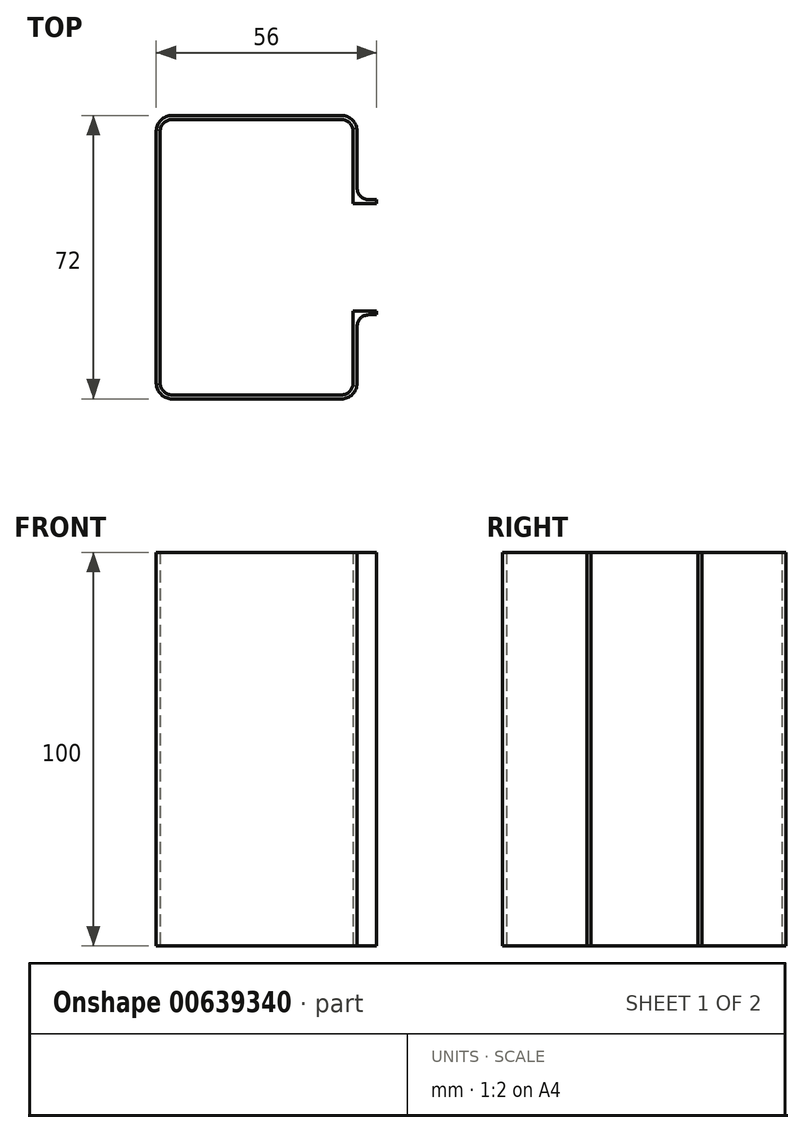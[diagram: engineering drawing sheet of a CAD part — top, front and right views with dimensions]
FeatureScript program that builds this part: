
annotation { "Feature Type Name" : "Feature", "Feature Type Description" : "" }
export const myFeature = defineFeature(function(context is Context, id is Id, definition is map)
    precondition{}
    {
        {
            var Q0;
            Q0=qCreatedBy(makeId("Top.planeOp"),FACE);
            var sketch = newSketch(context, id + "F0", { "sketchPlane" : qUnion([Q0])});
            skLineSegment(sketch, "E0.bottom", {"start": v(21.5, 35) * mm, "end": v(-21.5, 35) * mm});
            skLineSegment(sketch, "E0.top", {"start": v(21.5, -35) * mm, "end": v(-21.5, -35) * mm});
            skLineSegment(sketch, "E0.left", {"start": v(24.5, 32) * mm, "end": v(24.5, 13.63) * mm});
            skLineSegment(sketch, "E0.right", {"start": v(-24.5, 32) * mm, "end": v(-24.5, -32) * mm});
            skPoint(sketch, "E0.middle", {"position": v(0, 0) * mm});
            skPoint(sketch, "E1", {"position": v(24.5, 13.63) * mm});
            skPoint(sketch, "E2", {"position": v(24.5, -13.62) * mm});
            skLineSegment(sketch, "E3.trimOffspring", {"start": v(24.5, -13.62) * mm, "end": v(24.5, -32) * mm});
            skPoint(sketch, "E4.visualSharp", {"position": v(24.5, 35) * mm});
            skArc(sketch, "E4.filletArc", {"start": v(24.5, 32) * mm, "mid": v(23.62, 34.12) * mm, "end": v(21.5, 35) * mm});
            skPoint(sketch, "E5.visualSharp", {"position": v(-24.5, 35) * mm});
            skArc(sketch, "E5.filletArc", {"start": v(-21.5, 35) * mm, "mid": v(-23.62, 34.12) * mm, "end": v(-24.5, 32) * mm});
            skPoint(sketch, "E6.visualSharp", {"position": v(-24.5, -35) * mm});
            skArc(sketch, "E6.filletArc", {"start": v(-24.5, -32) * mm, "mid": v(-23.62, -34.12) * mm, "end": v(-21.5, -35) * mm});
            skPoint(sketch, "E7.visualSharp", {"position": v(24.5, -35) * mm});
            skArc(sketch, "E7.filletArc", {"start": v(21.5, -35) * mm, "mid": v(23.62, -34.12) * mm, "end": v(24.5, -32) * mm});
            skLineSegment(sketch, "E8", {"start": v(24.5, 13.63) * mm, "end": v(30.5, 13.63) * mm});
            skLineSegment(sketch, "E9", {"start": v(24.5, -13.62) * mm, "end": v(30.5, -13.62) * mm});
            skLineSegment(sketch, "E10.0", {"start": v(28.5, -14.62) * mm, "end": v(30.5, -14.62) * mm});
            skLineSegment(sketch, "E10.1", {"start": v(21.5, 36) * mm, "end": v(-21.5, 36) * mm});
            skArc(sketch, "E10.2", {"start": v(25.5, 32) * mm, "mid": v(24.33, 34.83) * mm, "end": v(21.5, 36) * mm});
            skLineSegment(sketch, "E10.3", {"start": v(25.5, 32) * mm, "end": v(25.5, 17.63) * mm});
            skLineSegment(sketch, "E10.4", {"start": v(28.5, 14.63) * mm, "end": v(30.5, 14.63) * mm});
            skArc(sketch, "E10.5", {"start": v(-21.5, 36) * mm, "mid": v(-24.33, 34.83) * mm, "end": v(-25.5, 32) * mm});
            skLineSegment(sketch, "E10.6", {"start": v(-25.5, 32) * mm, "end": v(-25.5, -32) * mm});
            skArc(sketch, "E10.7", {"start": v(-25.5, -32) * mm, "mid": v(-24.33, -34.83) * mm, "end": v(-21.5, -36) * mm});
            skLineSegment(sketch, "E10.8", {"start": v(21.5, -36) * mm, "end": v(-21.5, -36) * mm});
            skArc(sketch, "E10.9", {"start": v(21.5, -36) * mm, "mid": v(24.33, -34.83) * mm, "end": v(25.5, -32) * mm});
            skLineSegment(sketch, "E10.10", {"start": v(25.5, -17.62) * mm, "end": v(25.5, -32) * mm});
            skLineSegment(sketch, "E11", {"start": v(30.5, -13.62) * mm, "end": v(30.5, -14.62) * mm});
            skLineSegment(sketch, "E12", {"start": v(30.5, 14.63) * mm, "end": v(30.5, 13.63) * mm});
            skPoint(sketch, "E13.visualSharp", {"position": v(25.5, -14.62) * mm});
            skArc(sketch, "E13.filletArc", {"start": v(28.5, -14.62) * mm, "mid": v(26.38, -15.5) * mm, "end": v(25.5, -17.62) * mm});
            skPoint(sketch, "E14.visualSharp", {"position": v(25.5, 14.63) * mm});
            skArc(sketch, "E14.filletArc", {"start": v(25.5, 17.63) * mm, "mid": v(26.38, 15.5) * mm, "end": v(28.5, 14.63) * mm});
            skSolve(sketch);
        }
        {
            var Q0;
            Q0 = qSketchRegion(id + "F0", true);
            var Q1;
            Q1 = qSketchRegion(id + "FVOFp4DwUlX4e8R_1", true);
            extrude(context, id + "F1", {"entities" : qUnion([Q0, Q1]), "depth" : 100 * mm, "offsetDistance" : 25 * mm});
        }
    });
